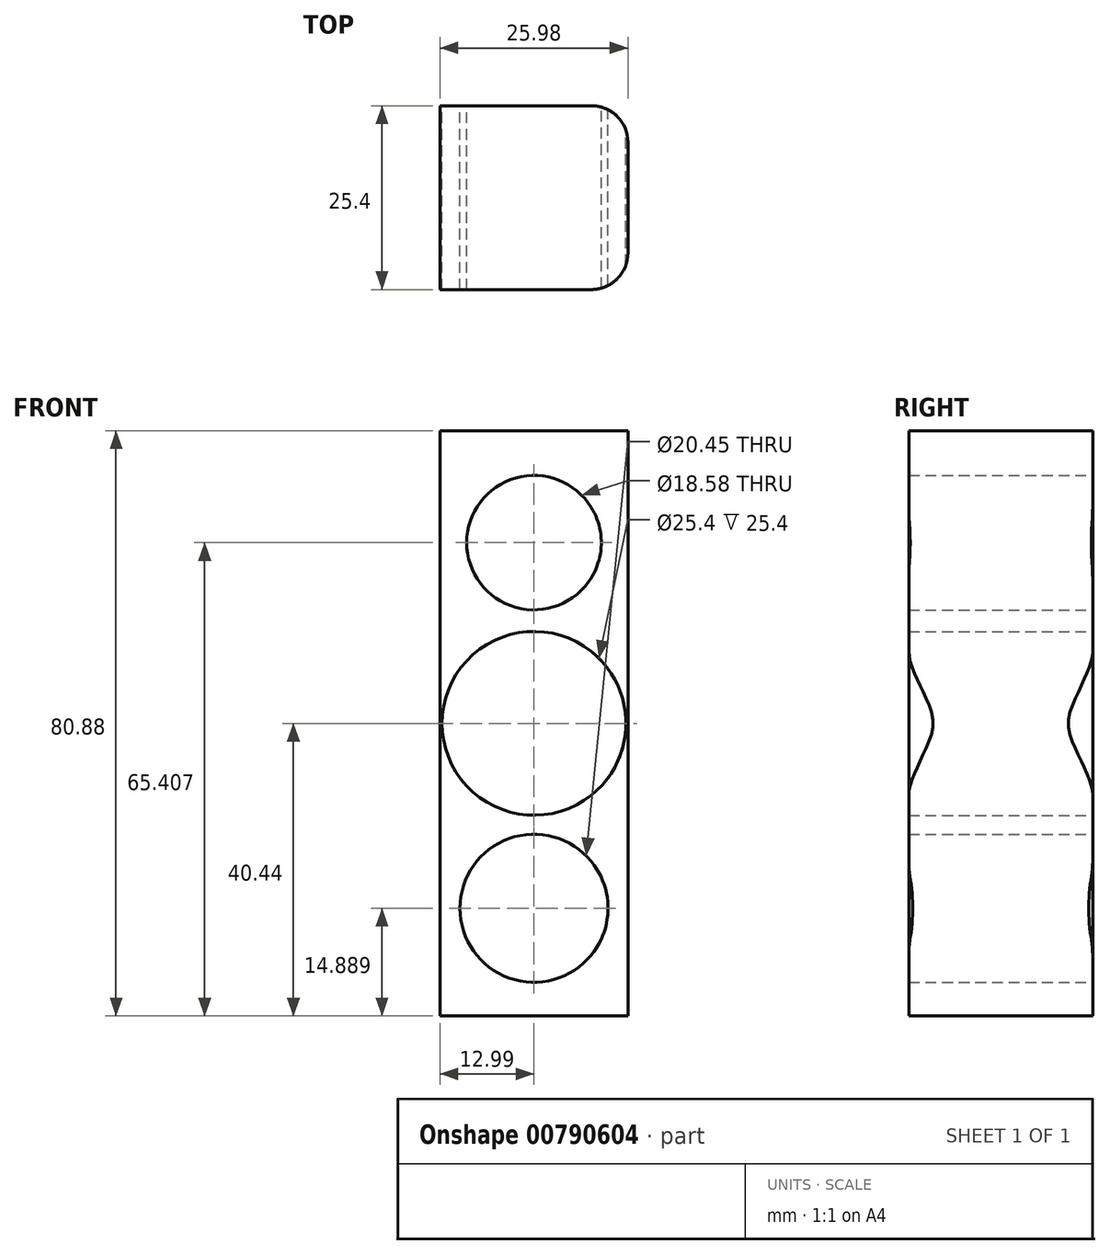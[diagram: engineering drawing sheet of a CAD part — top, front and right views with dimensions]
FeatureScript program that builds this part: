
annotation { "Feature Type Name" : "Feature", "Feature Type Description" : "" }
export const myFeature = defineFeature(function(context is Context, id is Id, definition is map)
    precondition{}
    {
        {
            var Q0;
            Q0=qCreatedBy(makeId("Front.planeOp"),FACE);
            var sketch = newSketch(context, id + "F0", { "sketchPlane" : qUnion([Q0])});
            skCircle(sketch, "E0", {"center": v(0, 0) * mm, "radius": 9.53 * mm});
            skSolve(sketch);
        }
        {
            var Q0;
            Q0=qCreatedBy(makeId("Front.planeOp"),FACE);
            var sketch = newSketch(context, id + "F1", { "sketchPlane" : qUnion([Q0])});
            skLineSegment(sketch, "E1.bottom", {"start": v(13, -40.44) * mm, "end": v(-13, -40.44) * mm});
            skLineSegment(sketch, "E1.top", {"start": v(13, 40.44) * mm, "end": v(-13, 40.44) * mm});
            skLineSegment(sketch, "E1.left", {"start": v(13, -40.44) * mm, "end": v(13, 40.44) * mm});
            skLineSegment(sketch, "E1.right", {"start": v(-13, -40.44) * mm, "end": v(-13, 40.44) * mm});
            skPoint(sketch, "E1.middle", {"position": v(0, 0) * mm});
            skSolve(sketch);
        }
        {
            var Q0;
            Q0=makeQuery(id+"F1.imprint","IMPRINT",FACE,{"disambiguationData":[TD([[makeQuery(id+"F1.imprint","IMPRINT",EDGE,{"derivedFrom":sQuery(id+"F1.wireOp",EDGE,"E1.bottom")}),-1.0]])]});
            var sketch = newSketch(context, id + "F2", { "sketchPlane" : qUnion([Q0])});
            skCircle(sketch, "E2", {"center": v(0, 24.97) * mm, "radius": 9.3 * mm});
            skCircle(sketch, "E3", {"center": v(0, -25.55) * mm, "radius": 10.23 * mm});
            skSolve(sketch);
        }
        {
            var Q0;
            Q0 = qSketchRegion(id + "FTPtkKL3vYEUBkY_0", true);
            var Q1;
            Q1=makeQuery(id+"F2.imprint","IMPRINT",FACE,{"disambiguationData":[TD([[makeQuery(id+"F2.imprint","IMPRINT",EDGE,{"derivedFrom":sQuery(id+"F2.wireOp",EDGE,"E2")}),-1.0]])]});
            extrude(context, id + "F3", {"entities" : qUnion([Q0, Q1]), "depth" : 25.4 * mm, "offsetDistance" : 25.4 * mm});
        }
        {
            var Q0;
            Q0=sQuery(id+"F0.wireOp",VERTEX,"E0.center");
            var Q1;
            Q1=makeQuery(id+"F3.opExtrude","SWEPT_BODY",BODY,{"disambiguationData":[OSD([sQuery(id+"F1.wireOp",EDGE,"E1.bottom"),sQuery(id+"F1.wireOp",EDGE,"E1.top"),sQuery(id+"F1.wireOp",EDGE,"E1.left"),sQuery(id+"F1.wireOp",EDGE,"E1.right"),sQuery(id+"F2.wireOp",EDGE,"E2"),sQuery(id+"F2.wireOp",EDGE,"E3")])]});
            hole(context, id + "F4", {"style" : HoleStyle.SIMPLE, "endStyle" : HoleEndStyle.THROUGH, "oppositeDirection" : true, "holeDiameter" : 25.4 * mm, "majorDiameter" : 6.35 * mm, "isTappedThrough" : true, "tappedDepth" : 12.7 * mm, "tapClearance" : 3, "locations" : qUnion([Q0]), "scope" : qUnion([Q1])});
        }
        {
            var Q0;
            Q0=makeQuery(id+"F4.hole-0.boolean.opBoolean","COPY",EDGE,{"derivedFrom":makeQuery(id+"F4.hole-0.opRevolve","SWEPT_EDGE",EDGE,{"disambiguationData":[OSD([sQuery(id+"F4.hole-0.sketch.wireOp",EDGE,"core_line_2"),sQuery(id+"F4.hole-0.sketch.wireOp",EDGE,"core_line_3")])]})});
            var Q1;
            Q1=makeQuery(id+"F3.opExtrude","CAP_EDGE",EDGE,{"disambiguationData":[OSD([sQuery(id+"F1.wireOp",EDGE,"E1.left")])],"isStart":true});
            var Q2;
            Q2=makeQuery(id+"F3.opExtrude","CAP_EDGE",EDGE,{"disambiguationData":[OSD([sQuery(id+"F1.wireOp",EDGE,"E1.left")])],"isStart":false});
            fillet(context, id + "F5", {"entities" : qUnion([Q0, Q1, Q2]), "radius" : 5.08 * mm, "tangentPropagation" : true, "allowEdgeOverflow" : false});
        }
    });
